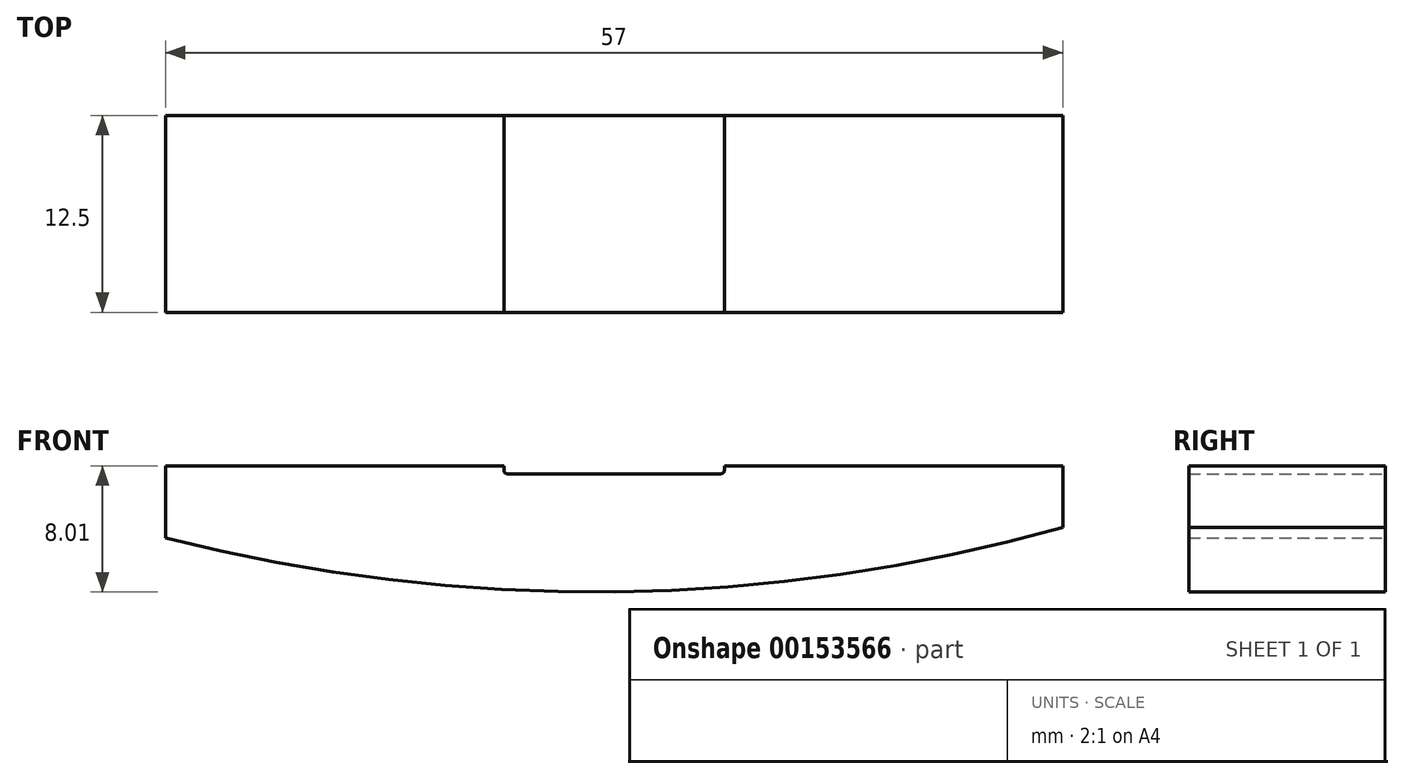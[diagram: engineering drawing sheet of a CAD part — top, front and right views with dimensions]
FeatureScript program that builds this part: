
annotation { "Feature Type Name" : "Feature", "Feature Type Description" : "" }
export const myFeature = defineFeature(function(context is Context, id is Id, definition is map)
    precondition{}
    {
        {
            var Q0;
            Q0=qCreatedBy(makeId("Front.planeOp"),FACE);
            var sketch = newSketch(context, id + "F0", { "sketchPlane" : qUnion([Q0])});
            skLineSegment(sketch, "E0", {"start": v(7, 4) * mm, "end": v(28.5, 4) * mm});
            skLineSegment(sketch, "E1", {"start": v(28.5, 4) * mm, "end": v(28.5, 0) * mm});
            skLineSegment(sketch, "E2", {"start": v(28.5, 0) * mm, "end": v(28.19, 0) * mm});
            skLineSegment(sketch, "E3", {"start": v(-28.5, 0) * mm, "end": v(-28.5, 4) * mm});
            skLineSegment(sketch, "E4", {"start": v(-28.5, 4) * mm, "end": v(-7, 4) * mm});
            skLineSegment(sketch, "E5", {"start": v(-28.5, -0.57) * mm, "end": v(-28.5, 0) * mm});
            skArc(sketch, "E6", {"start": v(-28.5, -0.57) * mm, "mid": v(0.04, -4) * mm, "end": v(28.5, 0.09) * mm});
            skPoint(sketch, "E6.first.point", {"position": v(0, -4) * mm});
            skPoint(sketch, "E6.second.point", {"position": v(0, 215.99) * mm});
            skPoint(sketch, "E6.third.point", {"position": v(108.52, 113.43) * mm});
            skPoint(sketch, "E7.end.orphan", {"position": v(28.5, -4) * mm});
            skPoint(sketch, "E8.orphan", {"position": v(-28.5, -4) * mm});
            skLineSegment(sketch, "E9", {"start": v(0, 3.5) * mm, "end": v(7, 3.5) * mm});
            skLineSegment(sketch, "E10", {"start": v(7, 3.5) * mm, "end": v(7, 4) * mm});
            skLineSegment(sketch, "E11", {"start": v(-7, 4) * mm, "end": v(-7, 3.5) * mm});
            skLineSegment(sketch, "E12", {"start": v(-7, 3.5) * mm, "end": v(0, 3.5) * mm});
            skPoint(sketch, "E13.orphan", {"position": v(0, 4) * mm});
            skPoint(sketch, "E14.start.orphan", {"position": v(0, 0) * mm});
            skSolve(sketch);
        }
        {
            var Q0;
            {var subQ3=sQuery(id+"F0.wireOp",EDGE,"E0");Q0=makeQuery(id+"F0.imprint","IMPRINT",FACE,{"disambiguationData":[TD([[makeQuery(id+"F0.imprint","IMPRINT",EDGE,{"derivedFrom":subQ3}),-1.0]])]});}
            extrude(context, id + "F1", {"entities" : qUnion([Q0]), "depth" : 12.5 * mm});
        }
        {
            var Q0;
            Q0=makeQuery(id+"F1.opExtrude","SWEPT_EDGE",EDGE,{"disambiguationData":[OSD([sQuery(id+"F0.wireOp",EDGE,"E11"),sQuery(id+"F0.wireOp",EDGE,"E12")])]});
            fillet(context, id + "F2", {"entities" : qUnion([Q0]), "radius" : 0.2 * mm, "tangentPropagation" : true, "allowEdgeOverflow" : false});
        }
        {
            var Q0;
            Q0=makeQuery(id+"F1.opExtrude","SWEPT_EDGE",EDGE,{"disambiguationData":[OSD([sQuery(id+"F0.wireOp",EDGE,"E9"),sQuery(id+"F0.wireOp",EDGE,"E10")])]});
            fillet(context, id + "F3", {"entities" : qUnion([Q0]), "radius" : 0.2 * mm, "tangentPropagation" : true, "allowEdgeOverflow" : false});
        }
    });
